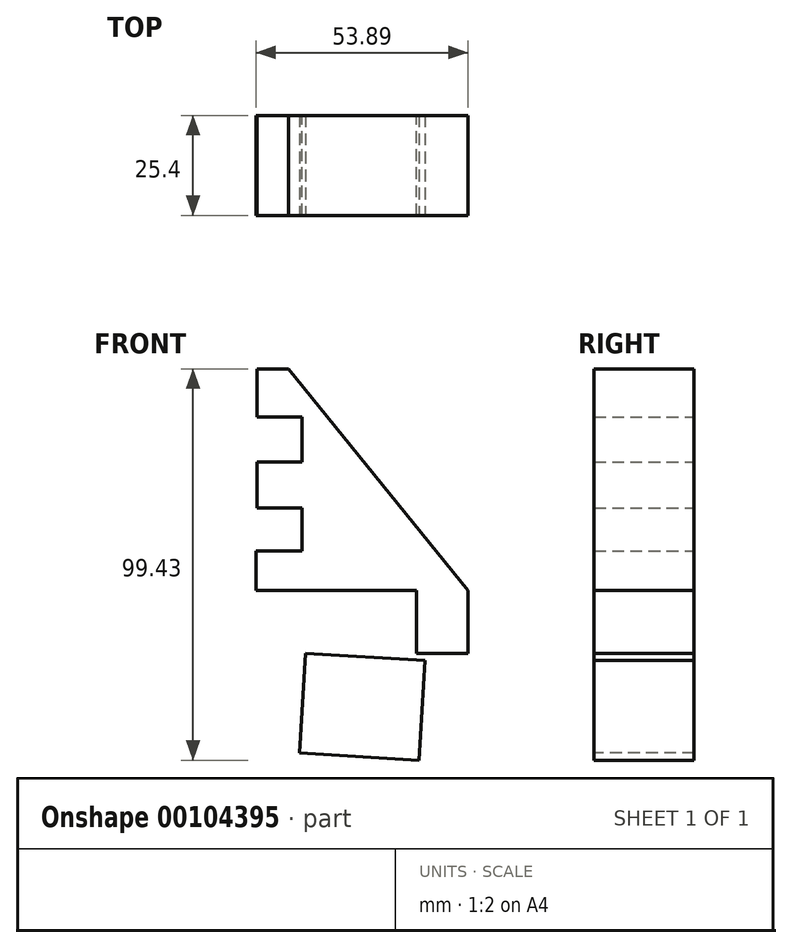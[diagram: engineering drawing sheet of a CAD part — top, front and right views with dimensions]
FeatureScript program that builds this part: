
annotation { "Feature Type Name" : "Feature", "Feature Type Description" : "" }
export const myFeature = defineFeature(function(context is Context, id is Id, definition is map)
    precondition{}
    {
        {
            var Q0;
            Q0=qCreatedBy(makeId("Front.planeOp"),FACE);
            var sketch = newSketch(context, id + "F0", { "sketchPlane" : qUnion([Q0])});
            skLineSegment(sketch, "E0", {"start": v(-11.4, 56.34) * mm, "end": v(-3.42, 56.34) * mm});
            skLineSegment(sketch, "E1", {"start": v(-3.42, 56.34) * mm, "end": v(42.2, 0) * mm});
            skLineSegment(sketch, "E2", {"start": v(42.2, 0) * mm, "end": v(-11.7, 0) * mm});
            skLineSegment(sketch, "E3", {"start": v(-11.7, 0) * mm, "end": v(-11.7, 10.13) * mm});
            skLineSegment(sketch, "E4", {"start": v(-11.7, 10.13) * mm, "end": v(0, 10.13) * mm});
            skLineSegment(sketch, "E5", {"start": v(0, 10.13) * mm, "end": v(0, 20.97) * mm});
            skLineSegment(sketch, "E6", {"start": v(0, 20.97) * mm, "end": v(-11.4, 20.97) * mm});
            skLineSegment(sketch, "E7", {"start": v(-11.4, 20.97) * mm, "end": v(-11.4, 32.66) * mm});
            skLineSegment(sketch, "E8", {"start": v(-11.4, 32.66) * mm, "end": v(0, 32.66) * mm});
            skLineSegment(sketch, "E9", {"start": v(0, 32.66) * mm, "end": v(0, 44.07) * mm});
            skLineSegment(sketch, "E10", {"start": v(0, 44.07) * mm, "end": v(-11.4, 44.07) * mm});
            skLineSegment(sketch, "E11", {"start": v(-11.4, 44.07) * mm, "end": v(-11.4, 56.34) * mm});
            skLineSegment(sketch, "E12", {"start": v(42.2, 0) * mm, "end": v(42.2, -15.95) * mm});
            skLineSegment(sketch, "E13", {"start": v(42.2, -15.95) * mm, "end": v(29.1, -15.95) * mm});
            skLineSegment(sketch, "E14", {"start": v(29.1, -15.95) * mm, "end": v(29.1, 0) * mm});
            skLineSegment(sketch, "E15", {"start": v(42.2, -15.95) * mm, "end": v(47.06, -15.95) * mm});
            skLineSegment(sketch, "E16", {"start": v(47.06, -15.95) * mm, "end": v(47.06, -21.82) * mm});
            skLineSegment(sketch, "E17", {"start": v(47.06, -21.82) * mm, "end": v(39.93, -21.82) * mm});
            skLineSegment(sketch, "E18", {"start": v(39.93, -21.82) * mm, "end": v(39.93, -41.5) * mm});
            skLineSegment(sketch, "E19", {"start": v(39.93, -41.5) * mm, "end": v(32.52, -41.5) * mm});
            skLineSegment(sketch, "E20", {"start": v(32.52, -41.5) * mm, "end": v(32.52, -23.65) * mm});
            skLineSegment(sketch, "E21", {"start": v(32.52, -23.65) * mm, "end": v(1.42, -23.65) * mm});
            skLineSegment(sketch, "E22", {"start": v(1.42, -23.65) * mm, "end": v(0.85, -15.95) * mm});
            skLineSegment(sketch, "E23", {"start": v(0.85, -15.95) * mm, "end": v(31.21, -17.73) * mm});
            skSolve(sketch);
        }
        {
            var Q0;
            Q0=sQuery(id+"F0.wireOp",EDGE,"E23");
            extrude(context, id + "F1", {"bodyType" : ToolBodyType.SURFACE, "surfaceEntities" : qUnion([Q0]), "depth" : 25.4 * mm});
        }
        {
            var Q0;
            Q0=makeQuery(id+"F0.imprint","IMPRINT",FACE,{"disambiguationData":[TD([[makeQuery(id+"F0.imprint","IMPRINT",EDGE,{"derivedFrom":sQuery(id+"F0.wireOp",EDGE,"E0")}),-1.0]])]});
            var Q1;
            {var subQ0=sQuery(id+"F0.wireOp",EDGE,"E12");Q1=makeQuery(id+"F0.imprint","IMPRINT",FACE,{"disambiguationData":[TD([[makeQuery(id+"F0.imprint","IMPRINT",EDGE,{"derivedFrom":subQ0}),-1.0]])]});}
            extrude(context, id + "F2", {"entities" : qUnion([Q0, Q1]), "depth" : 25.4 * mm});
        }
        {
            var Q0;
            Q0=makeQuery(id+"F1.opExtrude","SWEPT_FACE",FACE,{"disambiguationData":[OSD([sQuery(id+"F0.wireOp",EDGE,"E23")])]});
            extrude(context, id + "F3", {"entities" : qUnion([Q0]), "depth" : 25.4 * mm});
        }
    });
